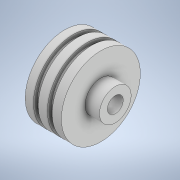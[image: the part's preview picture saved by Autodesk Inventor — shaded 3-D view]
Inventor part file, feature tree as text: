
AUTODESK INVENTOR PART (.ipt)
format: ipt  version: 2021 (Build 250183000, 183)  size: 178,688 bytes
history: native  units: mm
features: revolve x1, sketch x1
ambient origin geometry x8: Origin, YZ Plane, XZ Plane, XY Plane, X Axis, Y Axis, Z Axis, Center Point
bodies: Solid1 (feature_tree)
feature tree (2):
  revolve  "Revolution1"  [1 undecoded]
  sketch  "Sketch1"  dims[d0=38.5mm d1=22.5mm d2=38.5mm d3=6.0mm d4=11.0mm d5=7.0mm d6=2.8mm d7=3.6mm d8=7.0mm d9=2.8mm d10=3.6mm d12=12.0mm d13=30.0mm d14=27.5mm d15=21.0mm d16=23.0mm d17=1.745329mm d18=2.0mm d19=2.0mm d20=90.0deg]
note: 1 required parameter value undecoded (feature->parameter linkage not recoverable at this tier; creation-order binding heuristic only, values carry confidence <= 0.55)
